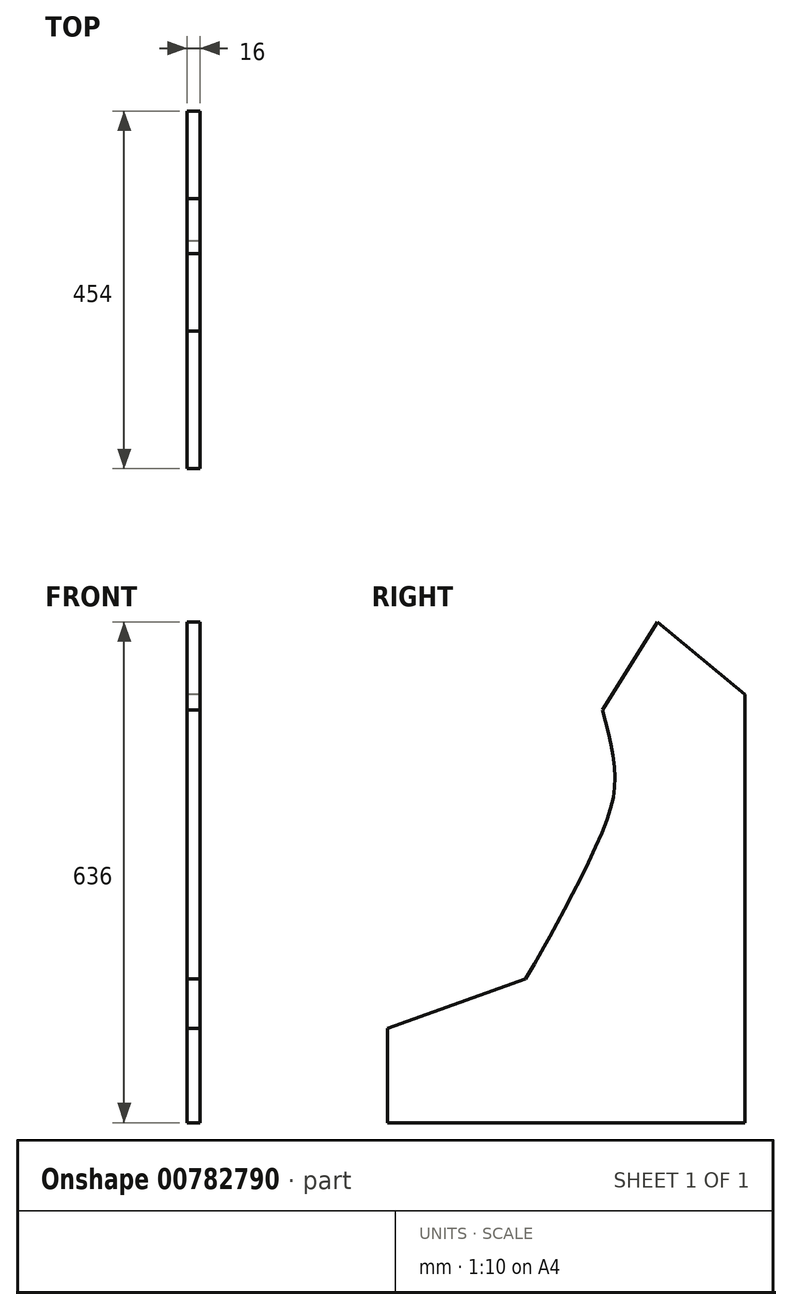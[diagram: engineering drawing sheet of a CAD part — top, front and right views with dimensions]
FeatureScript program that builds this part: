
annotation { "Feature Type Name" : "Feature", "Feature Type Description" : "" }
export const myFeature = defineFeature(function(context is Context, id is Id, definition is map)
    precondition{}
    {
        {
            var Q0;
            Q0=qCreatedBy(makeId("Right.planeOp"),FACE);
            var sketch = newSketch(context, id + "F0", { "sketchPlane" : qUnion([Q0])});
            skLineSegment(sketch, "E0", {"start": v(-58.17, -40.5) * mm, "end": v(-58.17, 503.5) * mm});
            skLineSegment(sketch, "E1", {"start": v(-58.17, 503.5) * mm, "end": v(-58.17, 483.55) * mm});
            skLineSegment(sketch, "E2.MirrorCS", {"start": v(-512.17, 79.5) * mm, "end": v(-337.4, 142) * mm});
            skLineSegment(sketch, "E3.MirrorCS", {"start": v(-239.27, 483.55) * mm, "end": v(-169.34, 595.5) * mm});
            skLineSegment(sketch, "E4.MirrorCS", {"start": v(-169.34, 595.5) * mm, "end": v(-58.17, 503.5) * mm});
            skLineSegment(sketch, "E5.MirrorCS", {"start": v(-512.17, -40.5) * mm, "end": v(-337.4, -40.5) * mm});
            skLineSegment(sketch, "E6.MirrorCS", {"start": v(-512.17, -40.5) * mm, "end": v(-512.17, 79.5) * mm});
            skLineSegment(sketch, "E7.MirrorCS", {"start": v(-512.17, -40.5) * mm, "end": v(-58.17, -40.5) * mm});
            skFitSpline(sketch, "E8", {"points": [v(-239.27, 483.55) * mm, v(-223.6, 405.44) * mm, v(-238.2, 332.39) * mm, v(-309.43, 189.94) * mm, v(-337.4, 142) * mm], "startDerivative": vector(88.95, -320.9) * mm, "endDerivative": vector(-147.19, -242.13) * mm});
            skSolve(sketch);
        }
        {
            var Q0;
            Q0 = qSketchRegion(id + "F0", true);
            extrude(context, id + "F1", {"entities" : qUnion([Q0]), "depth" : 16 * mm, "offsetDistance" : 25 * mm});
        }
    });
